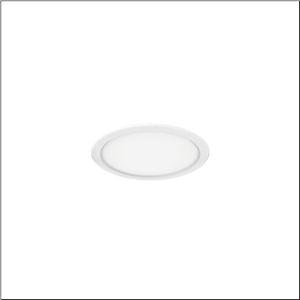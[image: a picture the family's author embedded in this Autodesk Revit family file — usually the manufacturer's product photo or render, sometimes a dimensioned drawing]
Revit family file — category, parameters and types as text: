
# Revit family: lunis_41_eco_51ds107d33a
name_source: partatom
category: Lighting Fixtures
units: mm (PartAtom-declared; Revit-internal decimal feet)

## family parameters
Cut with Voids When Loaded = No
Host = Face
Light Source = No
Part Type = Normal
Room Calculation Point = No
Round Connector Dimension = Use Diameter
Shared = No

## types (1)
- Lunis 41 ECO (1 x LED, 1400 lm, 14 W, 3000K)
    Apparent Load = 14 VA
    CIE Flux Codes = 47 80 97 100 100
    Color Rendering = 80
    Color Temperature = 3000K
    Default Elevation = 1800 mm
    Description = Lunis 41,  ECO, downlight, light emission: direct distribution, LED rated luminous flux: 1.400lm, light colour: 830, control gear: ECG, mains connection: 230V, AC, 50/60Hz, housing, round, of aluminium, coated, traffic white (RAL 9016), diameter: 166mm, recess depth: 54mm, protection rating (complete): IP20, protection rating (on room side): IP40, insulation class (complete): insulation class II (safety insulation), certification: CE, permissible ambient temperature for indoor applications: -20..+40°C, packaging unit: 1 piece
    Height = 0 mm  [stored 0 ft]
    Lamp = 1 x LED
    Lamp Light Flux = 1400 lm
    Lamp Power = 14 W
    Lamp count = 1
    Length = 165 mm
    Luminous efficacy = 100 lm/W
    Manufacturer = Siteco
    ModVariant = No
    Model = 51DS107D33A
    Mounting Place = Ceiling
    Mounting Type = Recessed
    Number of Poles = 1
    OnlyDefault = Yes
    Power Factor = 1
    Product Name = Lunis 41 ECO
    Product group = downlight
    ProductGroupID = 400
    Protection Class = Protection class II
    Protection Degree = IP 20
    RLX_Detail_Level = 1
    RLX_Emergency_Light_Flux = 0 lm
    RLX_Emergency_Type = 0
    RLX_Emergency_Type_DB = No
    RlxData = <blob elided: 25837 chars, md5=f8dfe0b6>
    Socket = socket
    Standby Power = 0 W
    System Light Flux = 1400 lm
    System Power = 14 W
    Type Comments = Product without accessories
    Type Image = l_1007041.jpg
    URL = http://relux.com
    VarID = ---
    Voltage = 0 V
    Weight = 0.00 kg
    Width = 0 mm  [stored 0 ft]

note: [stored X ft] marks values corroborated as IEEE doubles in the binary element streams (Revit-internal decimal feet)

## geometry (parser evidence)
native form markers: Blend x4, Sweep x11
no freeform markers — native parametric forms only
